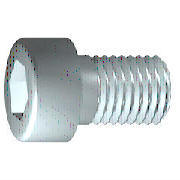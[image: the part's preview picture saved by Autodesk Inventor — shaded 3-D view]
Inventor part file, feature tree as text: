
AUTODESK INVENTOR PART (.ipt)
format: ipt  version: 2013 (Build 170138000, 138)  size: 181,248 bytes
history: native  units: mm (DEFAULTED — no unit token found)
features: sketch x2, extrude x1, plane x1, fillet x1
ambient origin geometry x7: Origin, YZ Plane, XY Plane, X Axis, Y Axis, Z Axis, Center Point
bodies: Solid1 (feature_tree), Body (feature_tree)
feature tree (5):
  extrude  "Slot"  Depth=0.306825mm
  plane  "Work Plane1"
  fillet  "Fillet2"  Radius=3.0mm
  sketch  "Sketch1"  dims[d1=18.0mm d2=0.306825mm d3=3.0mm]
  sketch  "Sketch2"  dims[d4=1.5mm d5=60.0deg d6=3.0mm d7=3.0mm d8=2.886751mm d9=5.5mm d10=90.0deg d11=10.0mm d12=0.0mm d13=18.0mm d14=0.0mm d15=0.306725mm d16=0.306725mm d17=0.3mm d19=0.0mm d26=25.0mm d27=45.0deg d28=0.0mm d29=0.0mm d30=0.1mm]
